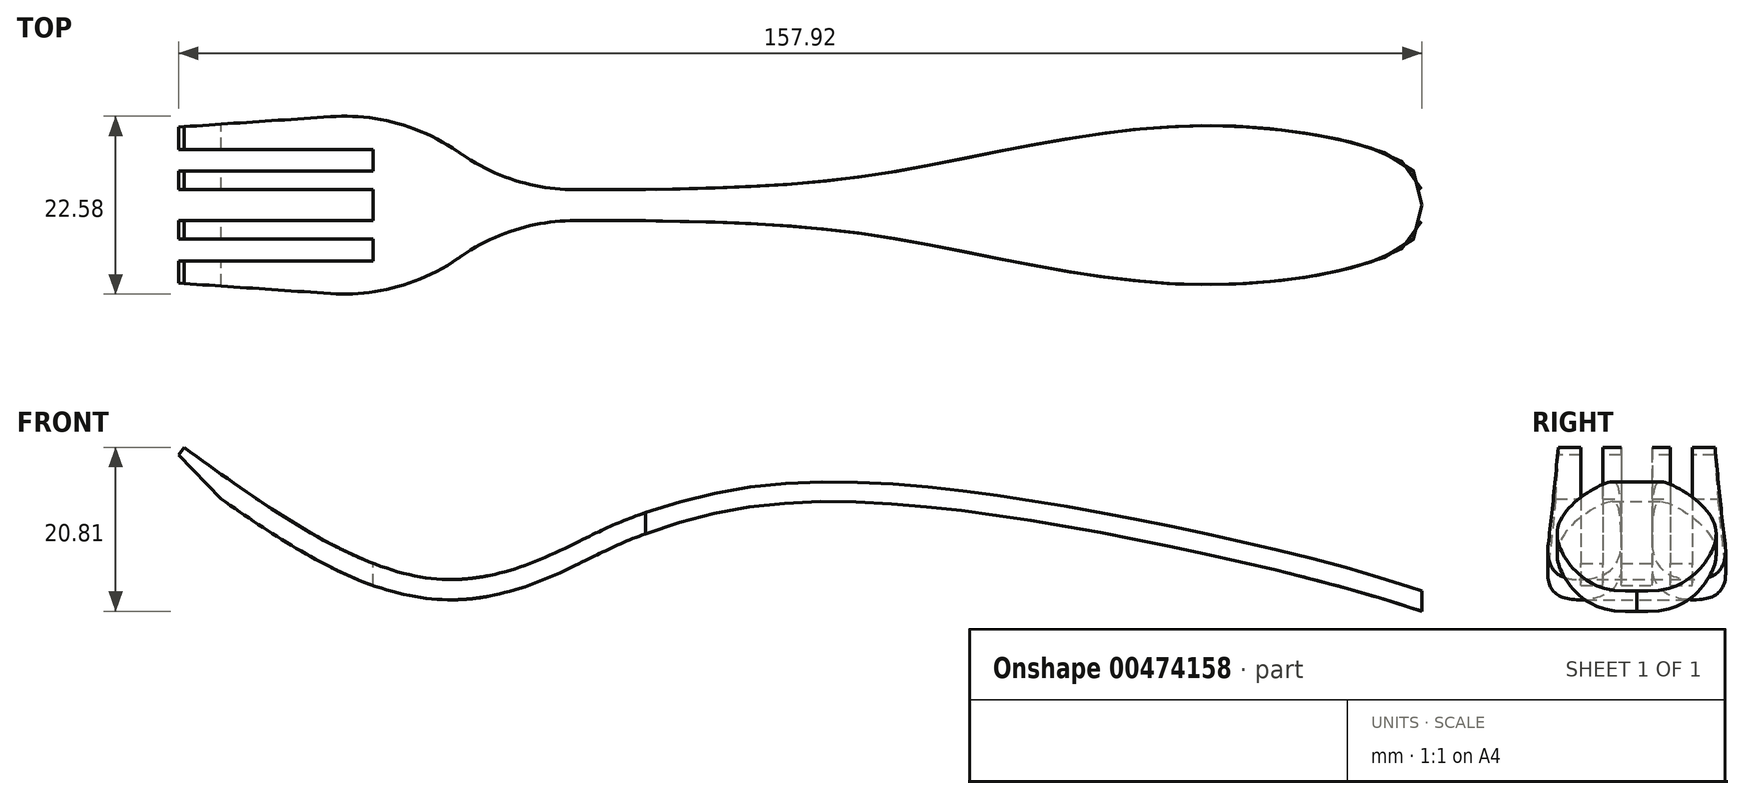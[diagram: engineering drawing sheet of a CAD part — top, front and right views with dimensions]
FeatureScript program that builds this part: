
annotation { "Feature Type Name" : "Feature", "Feature Type Description" : "" }
export const myFeature = defineFeature(function(context is Context, id is Id, definition is map)
    precondition{}
    {
        {
            var Q0;
            Q0=qCreatedBy(makeId("Front.planeOp"),FACE);
            var sketch = newSketch(context, id + "F0", { "sketchPlane" : qUnion([Q0])});
            skFitSpline(sketch, "E0", {"points": [v(0, 0) * mm, v(32.56, -16.74) * mm, v(51.2, -11.41) * mm, v(58.2, -8.42) * mm, v(78.51, -4.42) * mm, v(128.8, -10.75) * mm, v(165.1, -21.07) * mm], "startDerivative": vector(166, -120.1) * mm, "endDerivative": vector(166.5, -65.6) * mm});
            skFitSpline(sketch, "E1.0", {"points": [v(-1.49, -2.06) * mm, v(0.24, -3.3) * mm, v(3.75, -5.85) * mm, v(9.11, -9.56) * mm, v(14.55, -12.98) * mm, v(20.02, -15.9) * mm, v(24.6, -17.74) * mm, v(28.3, -18.74) * mm, v(30.6, -19.13) * mm, v(32.46, -19.3) * mm, v(34.3, -19.35) * mm, v(36.54, -19.22) * mm, v(39.12, -18.81) * mm, v(41.57, -18.21) * mm, v(43.9, -17.47) * mm, v(46.06, -16.64) * mm, v(48.07, -15.77) * mm, v(49.9, -14.9) * mm, v(51.27, -14.22) * mm, v(52.25, -13.73) * mm, v(53.15, -13.29) * mm, v(54.18, -12.8) * mm, v(55.3, -12.29) * mm, v(56.37, -11.83) * mm, v(57.47, -11.39) * mm, v(58.68, -10.94) * mm, v(60.07, -10.45) * mm, v(61.6, -9.94) * mm, v(63.87, -9.26) * mm, v(67.1, -8.42) * mm, v(70.87, -7.71) * mm, v(74.18, -7.28) * mm, v(76.82, -7.04) * mm, v(79.61, -6.9) * mm, v(82.57, -6.87) * mm, v(85.66, -6.95) * mm, v(89.96, -7.17) * mm, v(95.59, -7.66) * mm, v(102.61, -8.54) * mm, v(109.76, -9.64) * mm, v(116.9, -10.91) * mm, v(122.7, -12.06) * mm, v(127.2, -13) * mm, v(131.57, -13.94) * mm, v(136.79, -15.12) * mm, v(142.72, -16.58) * mm, v(148.36, -18.1) * mm, v(155.59, -20.27) * mm, v(160.76, -22.1) * mm, v(164.17, -23.44) * mm]});
            skLineSegment(sketch, "E2", {"start": v(0, 0) * mm, "end": v(-1.49, -2.06) * mm});
            skLineSegment(sketch, "E3", {"start": v(165.1, -21.07) * mm, "end": v(164.17, -23.44) * mm});
            skSolve(sketch);
        }
        {
            var Q0;
            Q0 = qSketchRegion(id + "F0", true);
            extrude(context, id + "F1", {"entities" : qUnion([Q0]), "depth" : 25.4 * mm});
        }
        {
            var Q0;
            Q0=qCreatedBy(makeId("Top.planeOp"),FACE);
            var sketch = newSketch(context, id + "F2", { "sketchPlane" : qUnion([Q0])});
            skPoint(sketch, "E4.0", {"position": v(-1.49, -12.7) * mm});
            skLineSegment(sketch, "E5", {"start": v(24.01, -12.7) * mm, "end": v(24.01, -14.67) * mm});
            skLineSegment(sketch, "E6", {"start": v(24.01, -14.67) * mm, "end": v(-3.37, -14.67) * mm});
            skLineSegment(sketch, "E7", {"start": v(-3.37, -14.67) * mm, "end": v(-3.37, -17) * mm});
            skLineSegment(sketch, "E8", {"start": v(-3.37, -17) * mm, "end": v(24.01, -17) * mm});
            skLineSegment(sketch, "E9", {"start": v(24.01, -17) * mm, "end": v(24.01, -19.77) * mm});
            skLineSegment(sketch, "E10", {"start": v(24.01, -19.77) * mm, "end": v(-3.37, -19.77) * mm});
            skLineSegment(sketch, "E11", {"start": v(-3.37, -19.77) * mm, "end": v(-3.37, -22.43) * mm});
            skLineSegment(sketch, "E12", {"start": v(-3.37, -22.43) * mm, "end": v(27.45, -24.54) * mm});
            skLineSegment(sketch, "E13", {"start": v(27.45, -24.54) * mm, "end": v(41.75, -14.67) * mm});
            skLineSegment(sketch, "E14", {"start": v(41.75, -14.67) * mm, "end": v(58.6, -14.67) * mm});
            skFitSpline(sketch, "E15", {"points": [v(58.6, -14.67) * mm, v(88.73, -16.7) * mm, v(128.93, -22.79) * mm, v(156.05, -17.18) * mm, v(157.22, -12.7) * mm], "startDerivative": vector(102.4, -1.91) * mm, "endDerivative": vector(0.41, 43.56) * mm});
            skLineSegment(sketch, "E16", {"start": v(24.01, -12.7) * mm, "end": v(157.22, -12.7) * mm, "construction": true});
            skLineSegment(sketch, "E17.MirrorCS", {"start": v(24.01, -12.7) * mm, "end": v(24.01, -10.73) * mm});
            skLineSegment(sketch, "E18.MirrorCS", {"start": v(-3.37, -10.73) * mm, "end": v(-3.37, -8.4) * mm});
            skLineSegment(sketch, "E19.MirrorCS", {"start": v(24.01, -8.4) * mm, "end": v(24.01, -5.63) * mm});
            skLineSegment(sketch, "E20.MirrorCS", {"start": v(-3.37, -5.63) * mm, "end": v(-3.37, -2.97) * mm});
            skLineSegment(sketch, "E21.MirrorCS", {"start": v(41.75, -10.73) * mm, "end": v(58.6, -10.73) * mm});
            skLineSegment(sketch, "E22.MirrorCS", {"start": v(24.01, -10.73) * mm, "end": v(-3.37, -10.73) * mm});
            skFitSpline(sketch, "E23.MirrorCS", {"points": [v(58.6, -10.73) * mm, v(88.73, -8.7) * mm, v(128.93, -2.61) * mm, v(156.05, -8.22) * mm, v(157.22, -12.7) * mm], "startDerivative": vector(102.4, 1.91) * mm, "endDerivative": vector(0.41, -43.56) * mm});
            skLineSegment(sketch, "E24.MirrorCS", {"start": v(27.45, -0.86) * mm, "end": v(41.75, -10.73) * mm});
            skLineSegment(sketch, "E25.MirrorCS", {"start": v(-3.37, -8.4) * mm, "end": v(24.01, -8.4) * mm});
            skLineSegment(sketch, "E26.MirrorCS", {"start": v(24.01, -5.63) * mm, "end": v(-3.37, -5.63) * mm});
            skLineSegment(sketch, "E27.MirrorCS", {"start": v(-3.37, -2.97) * mm, "end": v(27.45, -0.86) * mm});
            skLineSegment(sketch, "E28.bottom", {"start": v(-60.36, -110.28) * mm, "end": v(209.83, -110.28) * mm});
            skLineSegment(sketch, "E28.top", {"start": v(-60.36, 72.78) * mm, "end": v(209.83, 72.78) * mm});
            skLineSegment(sketch, "E28.left", {"start": v(-60.36, -110.28) * mm, "end": v(-60.36, 72.78) * mm});
            skLineSegment(sketch, "E28.right", {"start": v(209.83, -110.28) * mm, "end": v(209.83, 72.78) * mm});
            skSolve(sketch);
        }
        {
            var Q0;
            Q0 = qSketchRegion(id + "F2", true);
            extrude(context, id + "F3", {"entities" : qUnion([Q0]), "operationType" : NewBodyOperationType.REMOVE, "oppositeDirection" : true, "depth" : 25.4 * mm});
        }
        {
            var Q0;
            Q0=makeQuery(id+"F3.boolean.opBoolean","COPY",EDGE,{"derivedFrom":makeQuery(id+"F3.opExtrude","SWEPT_EDGE",EDGE,{"disambiguationData":[OSD([sQuery(id+"F2.wireOp",EDGE,"E24.MirrorCS"),sQuery(id+"F2.wireOp",EDGE,"E27.MirrorCS")])]})});
            var Q1;
            Q1=makeQuery(id+"F3.boolean.opBoolean","COPY",EDGE,{"derivedFrom":makeQuery(id+"F3.opExtrude","SWEPT_EDGE",EDGE,{"disambiguationData":[OSD([sQuery(id+"F2.wireOp",EDGE,"E21.MirrorCS"),sQuery(id+"F2.wireOp",EDGE,"E24.MirrorCS")])]})});
            var Q2;
            Q2=makeQuery(id+"F3.boolean.opBoolean","COPY",EDGE,{"derivedFrom":makeQuery(id+"F3.opExtrude","SWEPT_EDGE",EDGE,{"disambiguationData":[OSD([sQuery(id+"F2.wireOp",EDGE,"E13"),sQuery(id+"F2.wireOp",EDGE,"E14")])]})});
            var Q3;
            Q3=makeQuery(id+"F3.boolean.opBoolean","COPY",EDGE,{"derivedFrom":makeQuery(id+"F3.opExtrude","SWEPT_EDGE",EDGE,{"disambiguationData":[OSD([sQuery(id+"F2.wireOp",EDGE,"E12"),sQuery(id+"F2.wireOp",EDGE,"E13")])]})});
            fillet(context, id + "F4", {"entities" : qUnion([Q0, Q1, Q2, Q3]), "radius" : 25.4 * mm, "tangentPropagation" : true, "allowEdgeOverflow" : false});
        }
        {
            var Q0;
            {var subQ0=sQuery(id+"F0.wireOp",EDGE,"E1.0");var subQ1=sQuery(id+"F0.wireOp",EDGE,"E2");Q0=makeQuery(id+"F3.boolean.opBoolean","SPLIT",EDGE,{"disambiguationData":[TD([makeQuery(id+"F3.opExtrude","SWEPT_FACE",FACE,{"disambiguationData":[OSD([sQuery(id+"F2.wireOp",EDGE,"E26.MirrorCS")])]})])],"derivedFrom":makeQuery(id+"F1.opExtrude","SWEPT_EDGE",EDGE,{"disambiguationData":[OSD([subQ0,subQ1])]})});}
            var Q1;
            {var subQ0=sQuery(id+"F0.wireOp",EDGE,"E1.0");var subQ1=sQuery(id+"F0.wireOp",EDGE,"E2");Q1=makeQuery(id+"F3.boolean.opBoolean","SPLIT",EDGE,{"disambiguationData":[TD([makeQuery(id+"F3.opExtrude","SWEPT_FACE",FACE,{"disambiguationData":[OSD([sQuery(id+"F2.wireOp",EDGE,"E22.MirrorCS")])]})])],"derivedFrom":makeQuery(id+"F1.opExtrude","SWEPT_EDGE",EDGE,{"disambiguationData":[OSD([subQ0,subQ1])]})});}
            var Q2;
            {var subQ0=sQuery(id+"F0.wireOp",EDGE,"E1.0");var subQ1=sQuery(id+"F0.wireOp",EDGE,"E2");Q2=makeQuery(id+"F3.boolean.opBoolean","SPLIT",EDGE,{"disambiguationData":[TD([makeQuery(id+"F3.opExtrude","SWEPT_FACE",FACE,{"disambiguationData":[OSD([sQuery(id+"F2.wireOp",EDGE,"E6")])]})])],"derivedFrom":makeQuery(id+"F1.opExtrude","SWEPT_EDGE",EDGE,{"disambiguationData":[OSD([subQ0,subQ1])]})});}
            var Q3;
            {var subQ0=sQuery(id+"F0.wireOp",EDGE,"E1.0");var subQ1=sQuery(id+"F0.wireOp",EDGE,"E2");Q3=makeQuery(id+"F3.boolean.opBoolean","SPLIT",EDGE,{"disambiguationData":[TD([makeQuery(id+"F3.opExtrude","SWEPT_FACE",FACE,{"disambiguationData":[OSD([sQuery(id+"F2.wireOp",EDGE,"E10")])]})])],"derivedFrom":makeQuery(id+"F1.opExtrude","SWEPT_EDGE",EDGE,{"disambiguationData":[OSD([subQ0,subQ1])]})});}
            chamfer(context, id + "F5", {"entities" : qUnion([Q0, Q1, Q2, Q3]), "chamferType" : ChamferType.OFFSET_ANGLE, "width" : 7.62 * mm, "oppositeDirection" : false, "angle" : 10 * degree, "tangentPropagation" : true});
        }
    });
